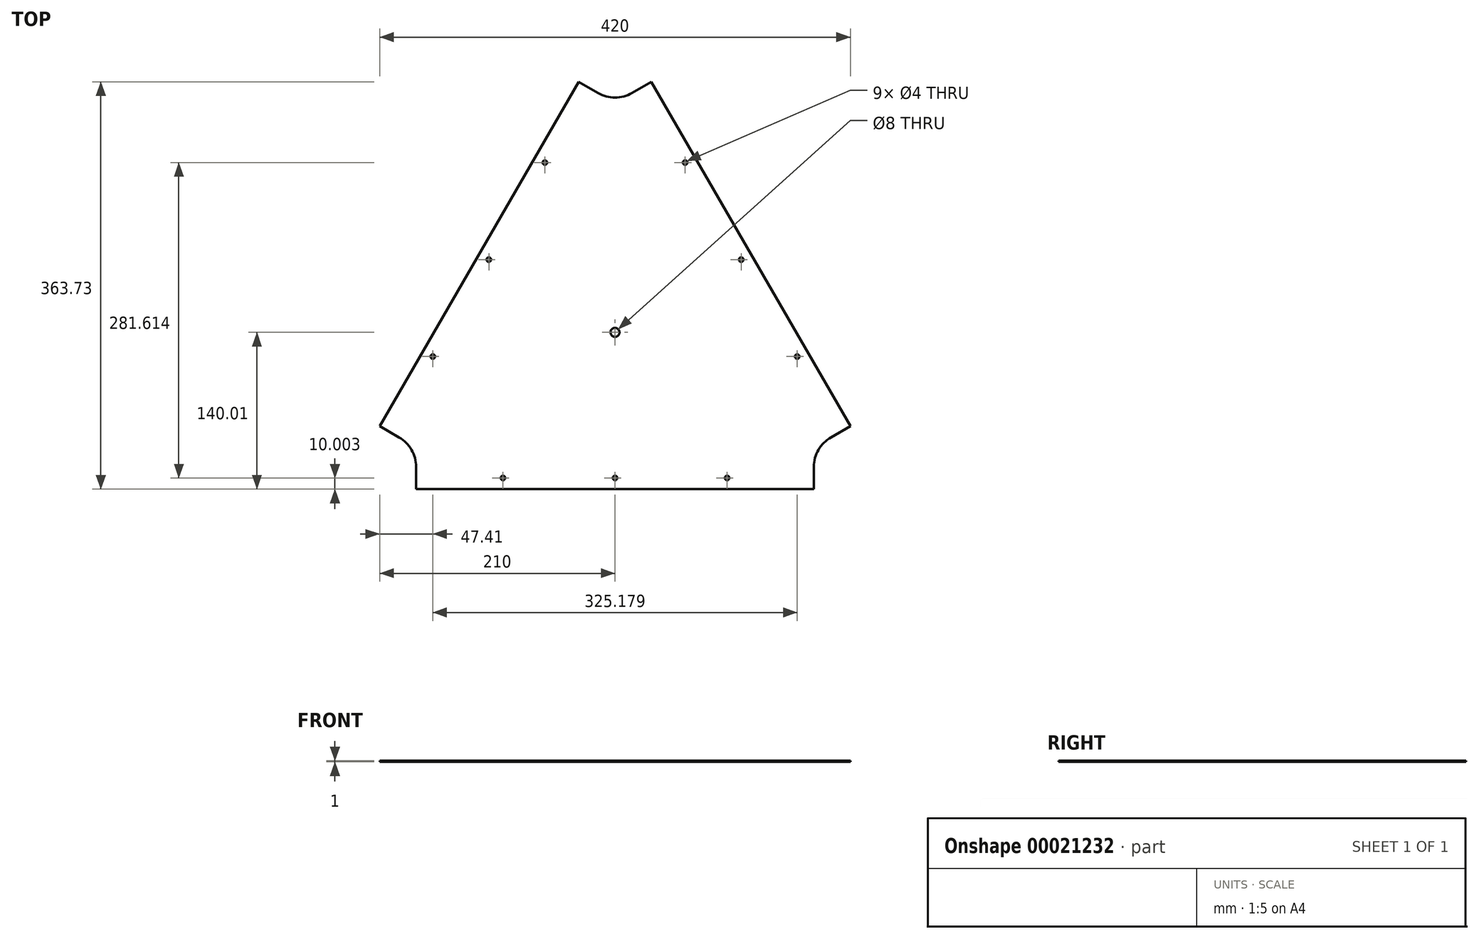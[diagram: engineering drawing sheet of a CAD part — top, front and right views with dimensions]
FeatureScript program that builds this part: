
annotation { "Feature Type Name" : "Feature", "Feature Type Description" : "" }
export const myFeature = defineFeature(function(context is Context, id is Id, definition is map)
    precondition{}
    {
        {
            var Q0;
            Q0=qCreatedBy(makeId("Top.planeOp"),FACE);
            var sketch = newSketch(context, id + "F0", { "sketchPlane" : qUnion([Q0])});
            skLineSegment(sketch, "E0.bottom", {"start": v(-177.5, -120) * mm, "end": v(177.5, -120) * mm, "construction": true});
            skLineSegment(sketch, "E0.top", {"start": v(-177.5, -140) * mm, "end": v(177.5, -140) * mm});
            skLineSegment(sketch, "E0.left", {"start": v(-177.5, -120) * mm, "end": v(-177.5, -140) * mm});
            skLineSegment(sketch, "E0.right", {"start": v(177.5, -120) * mm, "end": v(177.5, -140) * mm});
            skLineSegment(sketch, "E1", {"start": v(-177.5, -140) * mm, "end": v(-242.5, -140) * mm, "construction": true});
            skLineSegment(sketch, "E2", {"start": v(-242.5, -140) * mm, "end": v(-210, -83.72) * mm, "construction": true});
            skLineSegment(sketch, "E3", {"start": v(0, 280.01) * mm, "end": v(32.5, 223.72) * mm, "construction": true});
            skLineSegment(sketch, "E4", {"start": v(242.5, -140) * mm, "end": v(177.5, -140) * mm, "construction": true});
            skLineSegment(sketch, "E5", {"start": v(-210, -83.72) * mm, "end": v(-192.68, -93.72) * mm});
            skLineSegment(sketch, "E6", {"start": v(-192.68, -93.72) * mm, "end": v(-15.18, 213.72) * mm, "construction": true});
            skLineSegment(sketch, "E7", {"start": v(-15.18, 213.72) * mm, "end": v(-32.5, 223.72) * mm});
            skLineSegment(sketch, "E8", {"start": v(-210, -83.72) * mm, "end": v(-32.5, 223.72) * mm});
            skLineSegment(sketch, "E9", {"start": v(32.5, 223.72) * mm, "end": v(210, -83.72) * mm});
            skLineSegment(sketch, "E10", {"start": v(210, -83.72) * mm, "end": v(242.5, -140) * mm, "construction": true});
            skLineSegment(sketch, "E11", {"start": v(32.5, 223.72) * mm, "end": v(15.18, 213.72) * mm});
            skLineSegment(sketch, "E12", {"start": v(15.18, 213.72) * mm, "end": v(192.68, -93.72) * mm, "construction": true});
            skLineSegment(sketch, "E13", {"start": v(192.68, -93.72) * mm, "end": v(210, -83.72) * mm});
            skLineSegment(sketch, "E14", {"start": v(-103.93, 60) * mm, "end": v(0, 0) * mm, "construction": true});
            skLineSegment(sketch, "E15", {"start": v(0, 0) * mm, "end": v(103.93, 60) * mm, "construction": true});
            skLineSegment(sketch, "E16", {"start": v(0, 0) * mm, "end": v(0, -120) * mm, "construction": true});
            skLineSegment(sketch, "E17", {"start": v(-103.93, 60) * mm, "end": v(-121.25, 70) * mm, "construction": true});
            skLineSegment(sketch, "E18", {"start": v(103.93, 60) * mm, "end": v(121.25, 70) * mm, "construction": true});
            skLineSegment(sketch, "E19", {"start": v(0, -120) * mm, "end": v(0, -140) * mm, "construction": true});
            skCircle(sketch, "E20", {"center": v(-112.59, 65) * mm, "radius": 2 * mm});
            skCircle(sketch, "E21", {"center": v(112.59, 65) * mm, "radius": 2 * mm});
            skCircle(sketch, "E22", {"center": v(0, -130) * mm, "radius": 2 * mm});
            skLineSegment(sketch, "E23", {"start": v(-23.84, 218.72) * mm, "end": v(-201.34, -88.72) * mm, "construction": true});
            skLineSegment(sketch, "E24", {"start": v(-177.5, -130) * mm, "end": v(177.5, -130) * mm, "construction": true});
            skLineSegment(sketch, "E25", {"start": v(23.84, 218.72) * mm, "end": v(201.34, -88.72) * mm, "construction": true});
            skCircle(sketch, "E26", {"center": v(-162.59, -21.6) * mm, "radius": 2 * mm});
            skCircle(sketch, "E27.MirrorC", {"center": v(-62.59, 151.6) * mm, "radius": 2 * mm});
            skCircle(sketch, "E28.MirrorC", {"center": v(100, -130) * mm, "radius": 2 * mm});
            skCircle(sketch, "E29.MirrorC", {"center": v(-100, -130) * mm, "radius": 2 * mm});
            skCircle(sketch, "E30.MirrorC", {"center": v(162.59, -21.6) * mm, "radius": 2 * mm});
            skCircle(sketch, "E31.MirrorC", {"center": v(62.59, 151.6) * mm, "radius": 2 * mm});
            skCircle(sketch, "E32", {"center": v(0, 0) * mm, "radius": 4 * mm});
            skLineSegment(sketch, "E33", {"start": v(-32.5, 223.72) * mm, "end": v(0, 280.01) * mm, "construction": true});
            skArc(sketch, "E34", {"start": v(-177.5, -120) * mm, "mid": v(-181.57, -104.83) * mm, "end": v(-192.68, -93.72) * mm});
            skArc(sketch, "E35", {"start": v(-15.18, 213.72) * mm, "mid": v(0, 209.66) * mm, "end": v(15.18, 213.72) * mm});
            skArc(sketch, "E36", {"start": v(192.68, -93.72) * mm, "mid": v(181.57, -104.83) * mm, "end": v(177.5, -120) * mm});
            skSolve(sketch);
        }
        {
            var Q0;
            Q0=makeQuery(id+"F0.imprint","IMPRINT",FACE,{"disambiguationData":[TD([[makeQuery(id+"F0.imprint","IMPRINT",EDGE,{"derivedFrom":sQuery(id+"F0.wireOp",EDGE,"E0.top")}),1.0]])]});
            extrude(context, id + "F1", {"entities" : qUnion([Q0]), "depth" : 1 * mm});
        }
    });
